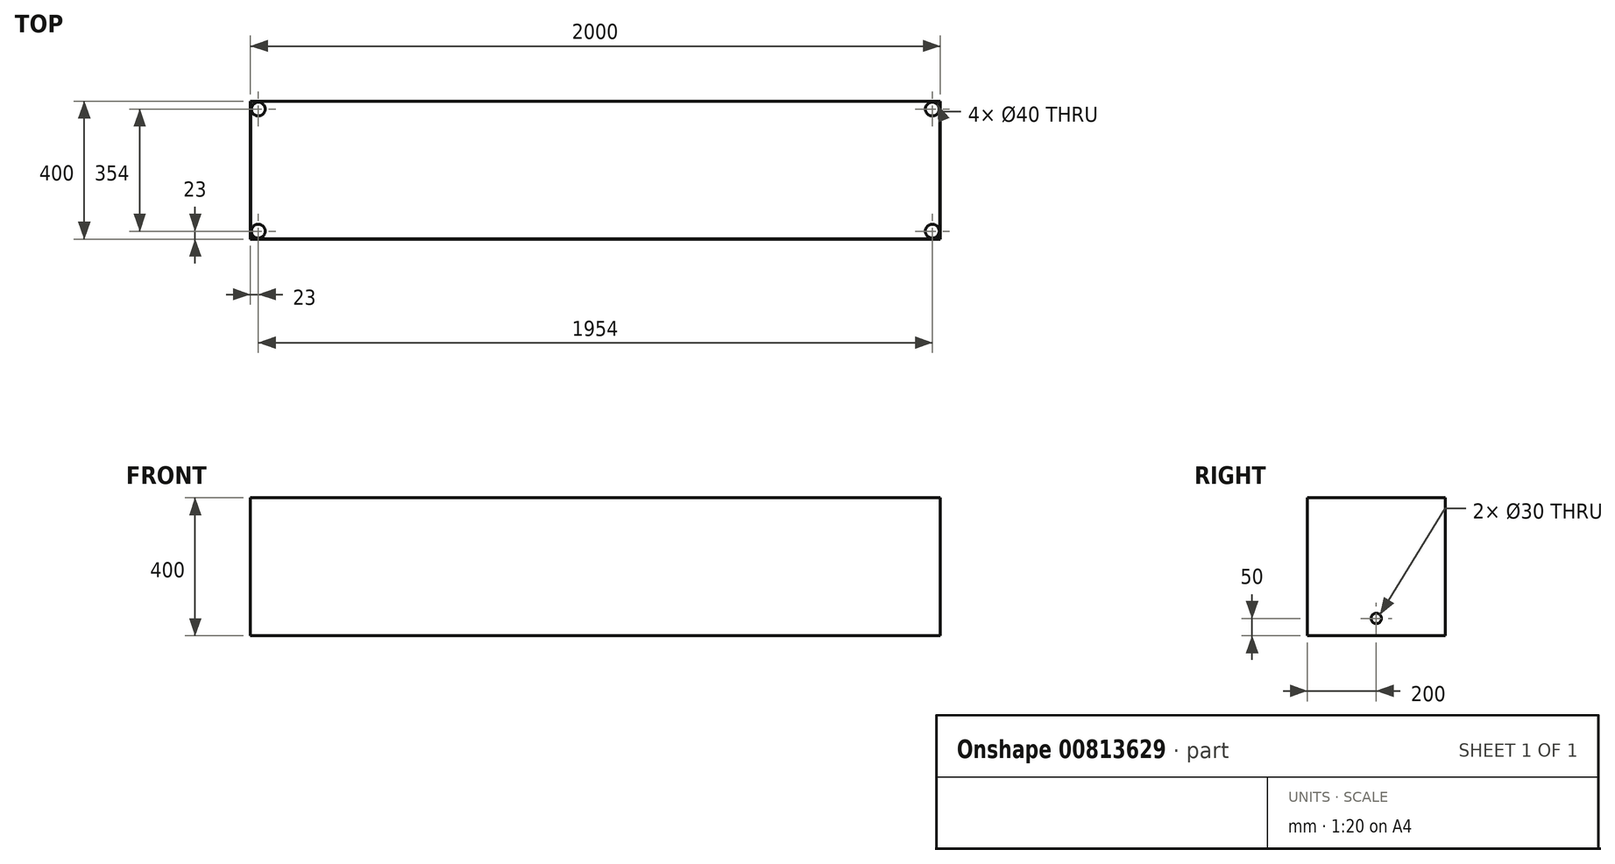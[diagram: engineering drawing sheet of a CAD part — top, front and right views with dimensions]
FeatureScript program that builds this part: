
annotation { "Feature Type Name" : "Feature", "Feature Type Description" : "" }
export const myFeature = defineFeature(function(context is Context, id is Id, definition is map)
    precondition{}
    {
        {
            var Q0;
            Q0=qCreatedBy(makeId("Top.planeOp"),FACE);
            var sketch = newSketch(context, id + "F0", { "sketchPlane" : qUnion([Q0])});
            skLineSegment(sketch, "E0.bottom", {"start": v(1000, 200) * mm, "end": v(-1000, 200) * mm});
            skLineSegment(sketch, "E0.top", {"start": v(1000, -200) * mm, "end": v(-1000, -200) * mm});
            skLineSegment(sketch, "E0.left", {"start": v(1000, 200) * mm, "end": v(1000, -200) * mm});
            skLineSegment(sketch, "E0.right", {"start": v(-1000, 200) * mm, "end": v(-1000, -200) * mm});
            skPoint(sketch, "E0.middle", {"position": v(0, 0) * mm});
            skSolve(sketch);
        }
        {
            var Q0;
            Q0=makeQuery(id+"F0.imprint","IMPRINT",FACE,{"disambiguationData":[TD([[makeQuery(id+"F0.imprint","IMPRINT",EDGE,{"derivedFrom":sQuery(id+"F0.wireOp",EDGE,"E0.bottom")}),1.0]])]});
            extrude(context, id + "F1", {"entities" : qUnion([Q0]), "depth" : 400 * mm, "offsetDistance" : 25 * mm});
        }
        {
            var Q0;
            Q0=makeQuery(id+"F1.opExtrude","CAP_FACE",FACE,{"disambiguationData":[OSD([sQuery(id+"F0.wireOp",EDGE,"E0.bottom"),sQuery(id+"F0.wireOp",EDGE,"E0.top"),sQuery(id+"F0.wireOp",EDGE,"E0.left"),sQuery(id+"F0.wireOp",EDGE,"E0.right")])],"isStart":false});
            shell(context, id + "F2", {"entities" : qUnion([Q0]), "thickness" : 1 * mm});
        }
        {
            var Q0;
            Q0=makeQuery(id+"F2.opShell","OFFSET_FACE",FACE,{"disambiguationData":[OSD([sQuery(id+"F0.wireOp",EDGE,"E0.bottom"),sQuery(id+"F0.wireOp",EDGE,"E0.top"),sQuery(id+"F0.wireOp",EDGE,"E0.left"),sQuery(id+"F0.wireOp",EDGE,"E0.right")])]});
            var sketch = newSketch(context, id + "F3", { "sketchPlane" : qUnion([Q0])});
            skCircle(sketch, "E1", {"center": v(-977, 177) * mm, "radius": 21.5 * mm});
            skCircle(sketch, "E2", {"center": v(-977, 177) * mm, "radius": 15.6 * mm});
            skCircle(sketch, "E3", {"center": v(977, 177) * mm, "radius": 22 * mm});
            skCircle(sketch, "E4.0", {"center": v(977, 177) * mm, "radius": 22.25 * mm});
            skCircle(sketch, "E5.0", {"center": v(977, 177) * mm, "radius": 18 * mm});
            skCircle(sketch, "E6", {"center": v(-977, -177) * mm, "radius": 22 * mm});
            skCircle(sketch, "E7.0", {"center": v(-977, -177) * mm, "radius": 18 * mm});
            skCircle(sketch, "E8", {"center": v(977, -177) * mm, "radius": 22 * mm});
            skCircle(sketch, "E9.0", {"center": v(977, -177) * mm, "radius": 18 * mm});
            skSolve(sketch);
        }
        {
            var Q0;
            Q0=sQuery(id+"F3.wireOp",EDGE,"E1");
            var Q1;
            Q1=sQuery(id+"F3.wireOp",EDGE,"E2");
            var Q2;
            Q2=sQuery(id+"F3.wireOp",EDGE,"E6");
            var Q3;
            Q3=sQuery(id+"F3.wireOp",EDGE,"E7.0");
            var Q4;
            Q4=sQuery(id+"F3.wireOp",EDGE,"E8");
            var Q5;
            Q5=sQuery(id+"F3.wireOp",EDGE,"E9.0");
            var Q6;
            Q6=sQuery(id+"F3.wireOp",EDGE,"E5.0");
            var Q7;
            Q7=sQuery(id+"F3.wireOp",EDGE,"E3");
            extrude(context, id + "F4", {"bodyType" : ToolBodyType.SURFACE, "surfaceEntities" : qUnion([Q0, Q1, Q2, Q3, Q4, Q5, Q6, Q7]), "depth" : 400 * mm, "offsetDistance" : 25 * mm});
        }
        {
            var Q0;
            Q0=sQuery(id+"F3.wireOp",VERTEX,"E4.0.center");
            var Q1;
            Q1=sQuery(id+"F3.wireOp",VERTEX,"E9.0.center");
            var Q2;
            Q2=sQuery(id+"F3.wireOp",VERTEX,"E1.center");
            var Q3;
            Q3=sQuery(id+"F3.wireOp",VERTEX,"E7.0.center");
            var Q4;
            Q4=makeQuery(id+"F1.opExtrude","SWEPT_BODY",BODY,{"disambiguationData":[OSD([sQuery(id+"F0.wireOp",EDGE,"E0.bottom"),sQuery(id+"F0.wireOp",EDGE,"E0.top"),sQuery(id+"F0.wireOp",EDGE,"E0.left"),sQuery(id+"F0.wireOp",EDGE,"E0.right")])]});
            hole(context, id + "F5", {"style" : HoleStyle.SIMPLE, "endStyle" : HoleEndStyle.THROUGH, "holeDiameter" : 40 * mm, "majorDiameter" : 5 * mm, "isTappedThrough" : true, "tappedDepth" : 12 * mm, "tapClearance" : 3, "locations" : qUnion([Q0, Q1, Q2, Q3]), "scope" : qUnion([Q4])});
        }
        {
            var Q0;
            Q0=makeQuery(id+"F1.opExtrude","SWEPT_FACE",FACE,{"disambiguationData":[OSD([sQuery(id+"F0.wireOp",EDGE,"E0.right")])]});
            var sketch = newSketch(context, id + "F6", { "sketchPlane" : qUnion([Q0])});
            skCircle(sketch, "E10", {"center": v(0, 50) * mm, "radius": 15 * mm});
            skCircle(sketch, "E11.0", {"center": v(0, 50) * mm, "radius": 15.25 * mm});
            skSolve(sketch);
        }
        {
            var Q0;
            Q0=sQuery(id+"F6.wireOp",EDGE,"E10");
            var Q1;
            Q1=sQuery(id+"F6.wireOp",EDGE,"E11.0");
            extrude(context, id + "F7", {"bodyType" : ToolBodyType.SURFACE, "surfaceEntities" : qUnion([Q0, Q1]), "oppositeDirection" : true, "depth" : 1600 * mm, "offsetDistance" : 25 * mm});
        }
        {
            var Q0;
            Q0=sQuery(id+"F6.wireOp",VERTEX,"E11.0.center");
            var Q1;
            Q1=makeQuery(id+"F1.opExtrude","SWEPT_BODY",BODY,{"disambiguationData":[OSD([sQuery(id+"F0.wireOp",EDGE,"E0.bottom"),sQuery(id+"F0.wireOp",EDGE,"E0.top"),sQuery(id+"F0.wireOp",EDGE,"E0.left"),sQuery(id+"F0.wireOp",EDGE,"E0.right")])]});
            hole(context, id + "F8", {"style" : HoleStyle.SIMPLE, "endStyle" : HoleEndStyle.THROUGH, "holeDiameter" : 30 * mm, "majorDiameter" : 5 * mm, "isTappedThrough" : true, "tappedDepth" : 12 * mm, "tapClearance" : 3, "locations" : qUnion([Q0]), "scope" : qUnion([Q1])});
        }
    });
